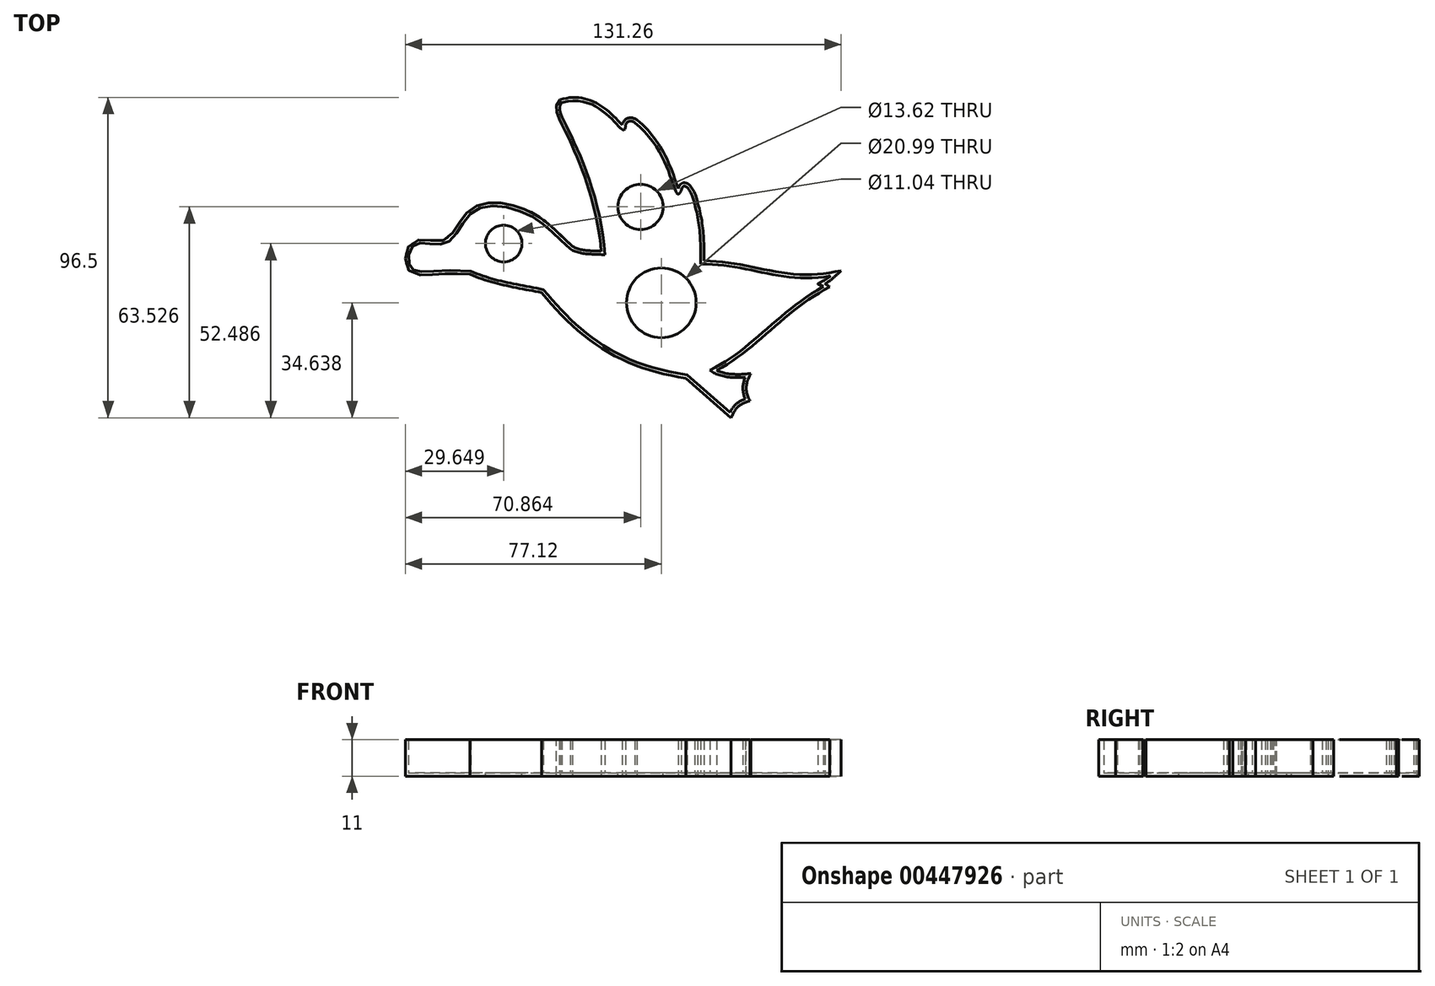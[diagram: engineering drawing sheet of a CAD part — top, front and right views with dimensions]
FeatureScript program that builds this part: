
annotation { "Feature Type Name" : "Feature", "Feature Type Description" : "" }
export const myFeature = defineFeature(function(context is Context, id is Id, definition is map)
    precondition{}
    {
        {
            var Q0;
            Q0=qCreatedBy(makeId("Top.planeOp"),FACE);
            var sketch = newSketch(context, id + "F0", { "sketchPlane" : qUnion([Q0])});
            skFitSpline(sketch, "E0", {"points": [v(-15.63, 49.63) * mm, v(2.87, 41.36) * mm, v(3.48, 42.24) * mm], "startDerivative": vector(39.5, 11.75) * mm, "endDerivative": vector(1.44, 6.1) * mm});
            skFitSpline(sketch, "E1", {"points": [v(6.33, 43.6) * mm, v(19.27, 22.05) * mm, v(20.22, 23.13) * mm], "startDerivative": vector(37.04, -29.48) * mm, "endDerivative": vector(3.82, 8.74) * mm});
            skFitSpline(sketch, "E2", {"points": [v(20.22, 23.13) * mm, v(24.27, 19) * mm], "startDerivative": vector(3.06, 12.3) * mm, "endDerivative": vector(0.17, -6.17) * mm});
            skFitSpline(sketch, "E3", {"points": [v(3.48, 42.24) * mm, v(6.33, 43.6) * mm], "startDerivative": vector(-0.9, 2.92) * mm, "endDerivative": vector(5.52, -3.9) * mm});
            skFitSpline(sketch, "E4", {"points": [v(24.27, 19) * mm, v(26.14, 0.96) * mm], "startDerivative": vector(5.47, -18.2) * mm, "endDerivative": vector(0, -17.89) * mm});
            skFitSpline(sketch, "E5", {"points": [v(26.14, 0.96) * mm, v(65.16, -2.61) * mm], "startDerivative": vector(40.8, 0.9) * mm, "endDerivative": vector(43.17, 7.58) * mm});
            skFitSpline(sketch, "E6", {"points": [v(65.16, -2.61) * mm, v(61.4, -5.02) * mm, v(63.06, -5.8) * mm], "startDerivative": vector(-8.24, -7.46) * mm, "endDerivative": vector(5.84, -3.9) * mm});
            skFitSpline(sketch, "E7", {"points": [v(63.06, -5.8) * mm, v(28.9, -30.98) * mm], "startDerivative": vector(-42.2, -23.7) * mm, "endDerivative": vector(-38.32, -18.83) * mm});
            skFitSpline(sketch, "E8", {"points": [v(28.9, -30.98) * mm, v(39.56, -33.12) * mm], "startDerivative": vector(8, -6.26) * mm, "endDerivative": vector(10.78, 1) * mm});
            skFitSpline(sketch, "E9", {"points": [v(39.56, -33.12) * mm, v(39.56, -39.64) * mm], "startDerivative": vector(-3, -6.45) * mm, "endDerivative": vector(2.89, -5.78) * mm});
            skFitSpline(sketch, "E10", {"points": [v(39.56, -39.64) * mm, v(34.95, -43.7) * mm], "startDerivative": vector(-7.95, -2.68) * mm, "endDerivative": vector(-2.48, -4.96) * mm});
            skLineSegment(sketch, "E11", {"start": v(34.95, -43.7) * mm, "end": v(22.07, -32.41) * mm});
            skFitSpline(sketch, "E12", {"points": [v(22.07, -32.41) * mm, v(-21.21, -6.73) * mm], "startDerivative": vector(-66.22, 9.55) * mm, "endDerivative": vector(-29.82, 36.1) * mm});
            skFitSpline(sketch, "E13", {"points": [v(-21.21, -6.73) * mm, v(-43.15, -1.13) * mm], "startDerivative": vector(-24.42, 5.2) * mm, "endDerivative": vector(-21.04, 9.3) * mm});
            skFitSpline(sketch, "E14", {"points": [v(-43.15, -1.13) * mm, v(-61.2, 0) * mm, v(-60.06, 6.82) * mm, v(-50.53, 7.3) * mm, v(-42.19, 16.97) * mm, v(-25.26, 15.6) * mm, v(-13.1, 5.57) * mm], "startDerivative": vector(-157.5, 17.23) * mm, "endDerivative": vector(70.32, -59.96) * mm});
            skFitSpline(sketch, "E15", {"points": [v(-13.1, 5.57) * mm, v(-2.77, 3.77) * mm], "startDerivative": vector(8.12, -5.74) * mm, "endDerivative": vector(10.2, -1.06) * mm});
            skFitSpline(sketch, "E16", {"points": [v(-2.77, 3.77) * mm, v(-14.82, 43.65) * mm, v(-15.63, 49.63) * mm], "startDerivative": vector(-4.02, 69.52) * mm, "endDerivative": vector(16.2, 16.13) * mm});
            skSolve(sketch);
        }
        {
            var Q0;
            Q0 = qSketchRegion(id + "F0", true);
            extrude(context, id + "F1", {"entities" : qUnion([Q0]), "depth" : 10 * mm});
        }
        {
            var Q0;
            Q0=makeQuery(id+"F1.opExtrude","CAP_FACE",FACE,{"disambiguationData":[OSD([sQuery(id+"F0.wireOp",EDGE,"E0"),sQuery(id+"F0.wireOp",EDGE,"E1"),sQuery(id+"F0.wireOp",EDGE,"E2"),sQuery(id+"F0.wireOp",EDGE,"E3"),sQuery(id+"F0.wireOp",EDGE,"E4"),sQuery(id+"F0.wireOp",EDGE,"E5"),sQuery(id+"F0.wireOp",EDGE,"E6"),sQuery(id+"F0.wireOp",EDGE,"E7"),sQuery(id+"F0.wireOp",EDGE,"E8"),sQuery(id+"F0.wireOp",EDGE,"E9"),sQuery(id+"F0.wireOp",EDGE,"E10"),sQuery(id+"F0.wireOp",EDGE,"E11"),sQuery(id+"F0.wireOp",EDGE,"E12"),sQuery(id+"F0.wireOp",EDGE,"E13"),sQuery(id+"F0.wireOp",EDGE,"E14"),sQuery(id+"F0.wireOp",EDGE,"E15"),sQuery(id+"F0.wireOp",EDGE,"E16")])],"isStart":false});
            shell(context, id + "F2", {"entities" : qUnion([Q0]), "thickness" : 1 * mm, "oppositeDirection" : true});
        }
        {
            var Q0;
            Q0=qCreatedBy(makeId("Top.planeOp"),FACE);
            var sketch = newSketch(context, id + "F3", { "sketchPlane" : qUnion([Q0])});
            skCircle(sketch, "E17", {"center": v(-33.21, 7.18) * mm, "radius": 5.52 * mm});
            skCircle(sketch, "E18", {"center": v(14.26, -10.67) * mm, "radius": 10.5 * mm});
            skCircle(sketch, "E19", {"center": v(8, 18.22) * mm, "radius": 6.8 * mm});
            skSolve(sketch);
        }
        {
            var Q0;
            Q0 = qSketchRegion(id + "F3", true);
            extrude(context, id + "F4", {"entities" : qUnion([Q0]), "operationType" : NewBodyOperationType.REMOVE, "oppositeDirection" : true, "depth" : 25 * mm});
        }
    });
